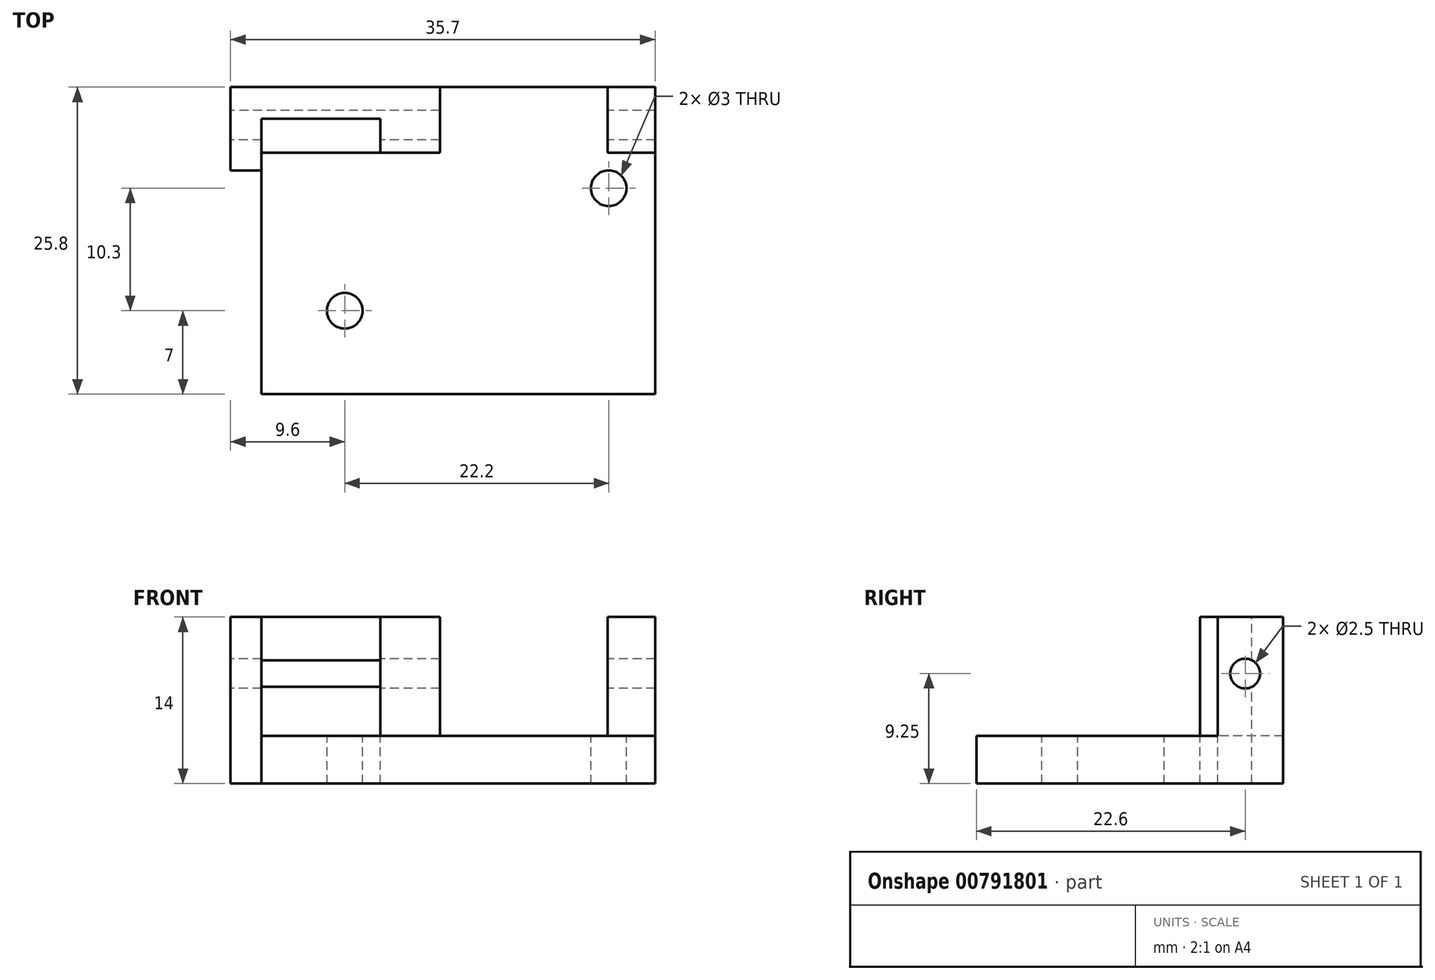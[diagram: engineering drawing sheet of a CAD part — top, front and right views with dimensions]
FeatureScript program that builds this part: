
annotation { "Feature Type Name" : "Feature", "Feature Type Description" : "" }
export const myFeature = defineFeature(function(context is Context, id is Id, definition is map)
    precondition{}
    {
        {
            var Q0;
            Q0=qCreatedBy(makeId("Top.planeOp"),FACE);
            var sketch = newSketch(context, id + "F0", { "sketchPlane" : qUnion([Q0])});
            skLineSegment(sketch, "E0.bottom", {"start": v(18.1, 10.15) * mm, "end": v(-18.1, 10.15) * mm});
            skLineSegment(sketch, "E0.top", {"start": v(18.1, -10.15) * mm, "end": v(-18.1, -10.15) * mm});
            skLineSegment(sketch, "E0.left", {"start": v(18.1, 10.15) * mm, "end": v(18.1, -10.15) * mm});
            skLineSegment(sketch, "E0.right", {"start": v(-18.1, 10.15) * mm, "end": v(-18.1, -10.15) * mm});
            skPoint(sketch, "E0.middle", {"position": v(0, 0) * mm});
            skCircle(sketch, "E1", {"center": v(-11.1, -3.15) * mm, "radius": 1.5 * mm});
            skCircle(sketch, "E2", {"center": v(11.1, 7.15) * mm, "radius": 1.5 * mm});
            skLineSegment(sketch, "E3", {"start": v(-11.1, -3.15) * mm, "end": v(11.1, -3.15) * mm});
            skLineSegment(sketch, "E4", {"start": v(11.1, 7.15) * mm, "end": v(11.1, -3.15) * mm});
            skLineSegment(sketch, "E5.bottom", {"start": v(-13.89, 10.15) * mm, "end": v(-11.58, 10.15) * mm});
            skLineSegment(sketch, "E6", {"start": v(-18.1, -10.15) * mm, "end": v(-28.1, -10.15) * mm});
            skLineSegment(sketch, "E7", {"start": v(-28.1, -10.15) * mm, "end": v(-28.1, 12.65) * mm});
            skLineSegment(sketch, "E8", {"start": v(-28.1, 12.65) * mm, "end": v(28.1, 12.65) * mm});
            skLineSegment(sketch, "E9", {"start": v(28.1, 12.65) * mm, "end": v(28.1, -10.15) * mm});
            skLineSegment(sketch, "E10", {"start": v(28.1, -10.15) * mm, "end": v(18.1, -10.15) * mm});
            skLineSegment(sketch, "E11", {"start": v(-28.1, 12.65) * mm, "end": v(-28.1, 15.65) * mm});
            skLineSegment(sketch, "E12", {"start": v(-28.1, 15.65) * mm, "end": v(28.1, 15.65) * mm});
            skLineSegment(sketch, "E13", {"start": v(28.1, 15.65) * mm, "end": v(28.1, 12.65) * mm});
            skLineSegment(sketch, "E14", {"start": v(-18.1, 10.15) * mm, "end": v(-18.1, 12.65) * mm});
            skLineSegment(sketch, "E15", {"start": v(-8.1, 10.15) * mm, "end": v(-8.1, 12.65) * mm});
            skSolve(sketch);
        }
        {
            var Q0;
            Q0=makeQuery(id+"F0.imprint","IMPRINT",FACE,{"disambiguationData":[TD([[makeQuery(id+"F0.imprint","IMPRINT",EDGE,{"derivedFrom":sQuery(id+"F0.wireOp",EDGE,"E8")}),1.0]])]});
            var Q1;
            {var subQ1=sQuery(id+"F0.wireOp",EDGE,"E0.left");Q1=makeQuery(id+"F0.imprint","IMPRINT",FACE,{"disambiguationData":[TD([[makeQuery(id+"F0.imprint","IMPRINT",EDGE,{"derivedFrom":subQ1}),1.0]])]});}
            var Q2;
            Q2=makeQuery(id+"F0.imprint","IMPRINT",FACE,{"disambiguationData":[TD([[makeQuery(id+"F0.imprint","IMPRINT",EDGE,{"derivedFrom":sQuery(id+"F0.wireOp",EDGE,"E0.top")}),-1.0]])]});
            var Q3;
            Q3=makeQuery(id+"F0.imprint","IMPRINT",FACE,{"disambiguationData":[TD([[makeQuery(id+"F0.imprint","IMPRINT",EDGE,{"derivedFrom":sQuery(id+"F0.wireOp",EDGE,"E0.right")}),-1.0]])]});
            var Q4;
            {var subQ0=sQuery(id+"F0.wireOp",EDGE,"E5.bottom");Q4=makeQuery(id+"F0.imprint","IMPRINT",FACE,{"disambiguationData":[TD([[makeQuery(id+"F0.imprint","IMPRINT",EDGE,{"derivedFrom":subQ0}),1.0]])]});}
            extrude(context, id + "F1", {"entities" : qUnion([Q0, Q1, Q2, Q3, Q4]), "depth" : -4 * mm, "offsetDistance" : 25 * mm});
        }
        {
            var Q0;
            Q0=makeQuery(id+"F0.imprint","IMPRINT",FACE,{"disambiguationData":[TD([[makeQuery(id+"F0.imprint","IMPRINT",EDGE,{"derivedFrom":sQuery(id+"F0.wireOp",EDGE,"E8")}),1.0]])]});
            var Q1;
            {var subQ3=sQuery(id+"F0.wireOp",EDGE,"E0.left");Q1=makeQuery(id+"F0.imprint","IMPRINT",FACE,{"disambiguationData":[TD([[makeQuery(id+"F0.imprint","IMPRINT",EDGE,{"derivedFrom":subQ3}),1.0]])]});}
            var Q2;
            Q2=makeQuery(id+"F0.imprint","IMPRINT",FACE,{"disambiguationData":[TD([[makeQuery(id+"F0.imprint","IMPRINT",EDGE,{"derivedFrom":sQuery(id+"F0.wireOp",EDGE,"E0.right")}),-1.0]])]});
            extrude(context, id + "F2", {"entities" : qUnion([Q0, Q1, Q2]), "operationType" : NewBodyOperationType.ADD, "depth" : 4 * mm, "offsetDistance" : 25 * mm});
        }
        {
            var Q0;
            {var subQ0=sQuery(id+"F0.wireOp",EDGE,"E11");var subQ1=sQuery(id+"F0.wireOp",EDGE,"E7");Q0=makeQuery(id+"F2.boolean.opBoolean","MERGE",FACE,{"derivedFrom":[makeQuery(id+"F1.opExtrude","SWEPT_FACE",FACE,{"disambiguationData":[OSD([subQ1,subQ0])]}),makeQuery(id+"F2.opExtrude","SWEPT_FACE",FACE,{"disambiguationData":[OSD([subQ1,subQ0])]})]});}
            var sketch = newSketch(context, id + "F3", { "sketchPlane" : qUnion([Q0])});
            skCircle(sketch, "E16", {"center": v(-12.45, 5.25) * mm, "radius": 1.25 * mm});
            skSolve(sketch);
        }
        {
            var Q0;
            {var subQ0=sQuery(id+"F0.wireOp",EDGE,"E13");var subQ1=sQuery(id+"F0.wireOp",EDGE,"E9");Q0=makeQuery(id+"F2.boolean.opBoolean","MERGE",FACE,{"derivedFrom":[makeQuery(id+"F1.opExtrude","SWEPT_FACE",FACE,{"disambiguationData":[OSD([subQ1,subQ0])]}),makeQuery(id+"F2.opExtrude","SWEPT_FACE",FACE,{"disambiguationData":[OSD([subQ1,subQ0])]})]});}
            extrude(context, id + "F4", {"entities" : qUnion([Q0]), "operationType" : NewBodyOperationType.REMOVE, "oppositeDirection" : true, "depth" : 13.1 * mm, "offsetDistance" : 25 * mm});
        }
        {
            var Q0;
            {var subQ0=sQuery(id+"F0.wireOp",EDGE,"E11");var subQ1=sQuery(id+"F0.wireOp",EDGE,"E7");Q0=makeQuery(id+"F2.boolean.opBoolean","MERGE",FACE,{"derivedFrom":[makeQuery(id+"F1.opExtrude","SWEPT_FACE",FACE,{"disambiguationData":[OSD([subQ1,subQ0])]}),makeQuery(id+"F2.opExtrude","SWEPT_FACE",FACE,{"disambiguationData":[OSD([subQ1,subQ0])]})]});}
            extrude(context, id + "F5", {"entities" : qUnion([Q0]), "operationType" : NewBodyOperationType.REMOVE, "oppositeDirection" : true, "depth" : 7.4 * mm, "offsetDistance" : 25 * mm});
        }
        {
            var Q0;
            {var subQ0=sQuery(id+"F0.wireOp",EDGE,"E15");var subQ1=sQuery(id+"F0.wireOp",EDGE,"E14");var subQ2=sQuery(id+"F0.wireOp",EDGE,"E8");var subQ3=sQuery(id+"F0.wireOp",EDGE,"E0.right");Q0=makeQuery(id+"FGGsML63CChQTcK_1.boolean.opBoolean","SPLIT",FACE,{"disambiguationData":[TD([makeQuery(id+"F2.opExtrude","CAP_FACE",FACE,{"disambiguationData":[OSD([sQuery(id+"F0.wireOp",EDGE,"E0.bottom"),sQuery(id+"F0.wireOp",EDGE,"E0.left"),subQ3,sQuery(id+"F0.wireOp",EDGE,"E6"),sQuery(id+"F0.wireOp",EDGE,"E7"),subQ2,sQuery(id+"F0.wireOp",EDGE,"E9"),sQuery(id+"F0.wireOp",EDGE,"E10"),sQuery(id+"F0.wireOp",EDGE,"E11"),sQuery(id+"F0.wireOp",EDGE,"E12"),sQuery(id+"F0.wireOp",EDGE,"E13"),subQ1,subQ0])],"isStart":false})])],"derivedFrom":makeQuery(id+"F2.opExtrude","SWEPT_FACE",FACE,{"disambiguationData":[OSD([subQ2])]})});}
            extrude(context, id + "F6", {"entities" : qUnion([Q0]), "operationType" : NewBodyOperationType.REMOVE, "oppositeDirection" : true, "depth" : 0.35 * mm, "offsetDistance" : 25 * mm});
        }
        {
            var Q0;
            Q0=makeQuery(id+"F2.opExtrude","CAP_FACE",FACE,{"disambiguationData":[OSD([sQuery(id+"F0.wireOp",EDGE,"E0.bottom"),sQuery(id+"F0.wireOp",EDGE,"E0.left"),sQuery(id+"F0.wireOp",EDGE,"E0.right"),sQuery(id+"F0.wireOp",EDGE,"E6"),sQuery(id+"F0.wireOp",EDGE,"E7"),sQuery(id+"F0.wireOp",EDGE,"E8"),sQuery(id+"F0.wireOp",EDGE,"E9"),sQuery(id+"F0.wireOp",EDGE,"E10"),sQuery(id+"F0.wireOp",EDGE,"E11"),sQuery(id+"F0.wireOp",EDGE,"E12"),sQuery(id+"F0.wireOp",EDGE,"E13"),sQuery(id+"F0.wireOp",EDGE,"E14"),sQuery(id+"F0.wireOp",EDGE,"E15")])],"isStart":false});
            extrude(context, id + "F7", {"entities" : qUnion([Q0]), "operationType" : NewBodyOperationType.ADD, "depth" : 6 * mm, "offsetDistance" : 25 * mm});
        }
        {
            var Q0;
            Q0=makeQuery(id+"F3.imprint","IMPRINT",FACE,{"disambiguationData":[TD([[makeQuery(id+"F3.imprint","IMPRINT",EDGE,{"derivedFrom":sQuery(id+"F3.wireOp",EDGE,"E16")}),1.0]])]});
            extrude(context, id + "F8", {"entities" : qUnion([Q0]), "operationType" : NewBodyOperationType.REMOVE, "oppositeDirection" : true, "depth" : 51.2 * mm, "offsetDistance" : 25 * mm});
        }
        {
            var Q0;
            Q0=makeQuery(id+"F7.opExtrude","CAP_FACE",FACE,{"disambiguationData":[OSD([sQuery(id+"F0.wireOp",EDGE,"E0.bottom"),sQuery(id+"F0.wireOp",EDGE,"E0.left"),sQuery(id+"F0.wireOp",EDGE,"E0.right"),sQuery(id+"F0.wireOp",EDGE,"E6"),sQuery(id+"F0.wireOp",EDGE,"E7"),sQuery(id+"F0.wireOp",EDGE,"E8"),sQuery(id+"F0.wireOp",EDGE,"E9"),sQuery(id+"F0.wireOp",EDGE,"E10"),sQuery(id+"F0.wireOp",EDGE,"E11"),sQuery(id+"F0.wireOp",EDGE,"E12"),sQuery(id+"F0.wireOp",EDGE,"E13"),sQuery(id+"F0.wireOp",EDGE,"E14"),sQuery(id+"F0.wireOp",EDGE,"E15")])],"isStart":false});
            var sketch = newSketch(context, id + "F9", { "sketchPlane" : qUnion([Q0])});
            skLineSegment(sketch, "E17.bottom", {"start": v(11, 15.65) * mm, "end": v(-3.1, 15.65) * mm});
            skLineSegment(sketch, "E17.top", {"start": v(11, 10.15) * mm, "end": v(-3.1, 10.15) * mm});
            skLineSegment(sketch, "E17.left", {"start": v(11, 15.65) * mm, "end": v(11, 10.15) * mm});
            skLineSegment(sketch, "E17.right", {"start": v(-3.1, 15.65) * mm, "end": v(-3.1, 10.15) * mm});
            skLineSegment(sketch, "E18.bottom", {"start": v(-18.1, -10.15) * mm, "end": v(-20.7, -10.15) * mm});
            skLineSegment(sketch, "E18.top", {"start": v(-18.1, 8.65) * mm, "end": v(-20.7, 8.65) * mm});
            skLineSegment(sketch, "E18.left", {"start": v(-18.1, -10.15) * mm, "end": v(-18.1, 8.65) * mm});
            skLineSegment(sketch, "E18.right", {"start": v(-20.7, -10.15) * mm, "end": v(-20.7, 8.65) * mm});
            skSolve(sketch);
        }
        {
            var Q0;
            Q0=makeQuery(id+"F9.imprint","IMPRINT",FACE,{"disambiguationData":[TD([[makeQuery(id+"F9.imprint","IMPRINT",EDGE,{"derivedFrom":sQuery(id+"F9.wireOp",EDGE,"E17.bottom")}),-1.0]])]});
            var Q1;
            Q1=makeQuery(id+"F9.imprint","IMPRINT",FACE,{"disambiguationData":[TD([[makeQuery(id+"F9.imprint","IMPRINT",EDGE,{"derivedFrom":sQuery(id+"F9.wireOp",EDGE,"E18.bottom")}),-1.0]])]});
            extrude(context, id + "F10", {"entities" : qUnion([Q0, Q1]), "operationType" : NewBodyOperationType.REMOVE, "oppositeDirection" : true, "depth" : 10 * mm, "offsetDistance" : 25 * mm});
        }
        {
            var Q0;
            Q0=makeQuery(id+"F9.imprint","IMPRINT",FACE,{"disambiguationData":[TD([[makeQuery(id+"F9.imprint","IMPRINT",EDGE,{"derivedFrom":sQuery(id+"F9.wireOp",EDGE,"E18.bottom")}),-1.0]])]});
            extrude(context, id + "F11", {"entities" : qUnion([Q0]), "operationType" : NewBodyOperationType.REMOVE, "oppositeDirection" : true, "depth" : 25 * mm, "offsetDistance" : 25 * mm});
        }
    });
